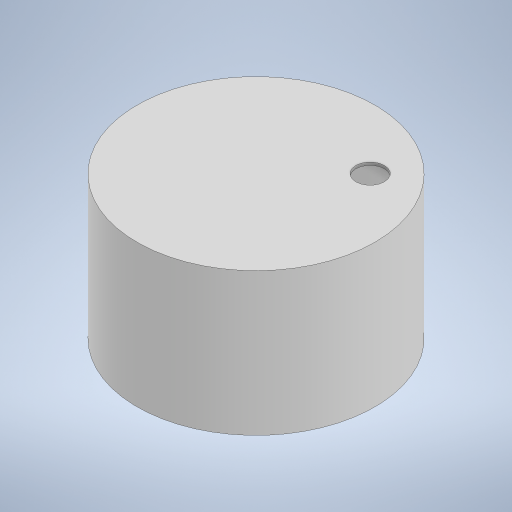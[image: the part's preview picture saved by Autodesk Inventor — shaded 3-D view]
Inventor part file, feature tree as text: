
AUTODESK INVENTOR PART (.ipt)
format: ipt  version: 2023 (Build 270158000, 158)  size: 208,896 bytes
history: native  units: mm
features: extrude x4, sketch x4, other x1
ambient origin geometry x8: Origin, YZ Plane, XZ Plane, XY Plane, X Axis, Y Axis, Z Axis, Center Point
bodies: Body1 (feature_tree)
feature tree (9):
  other  "ソリッド1"
  extrude  "押し出し1"  Depth=250.0mm
  extrude  "押し出し2"  Depth=3.0mm TaperAngle=0.0deg
  extrude  "押し出し3"  Depth=250.0mm
  extrude  "押し出し4"  Depth=235.0mm
  sketch  "スケッチ1"
  sketch  "スケッチ2"
  sketch  "スケッチ3"
  sketch  "スケッチ4"
